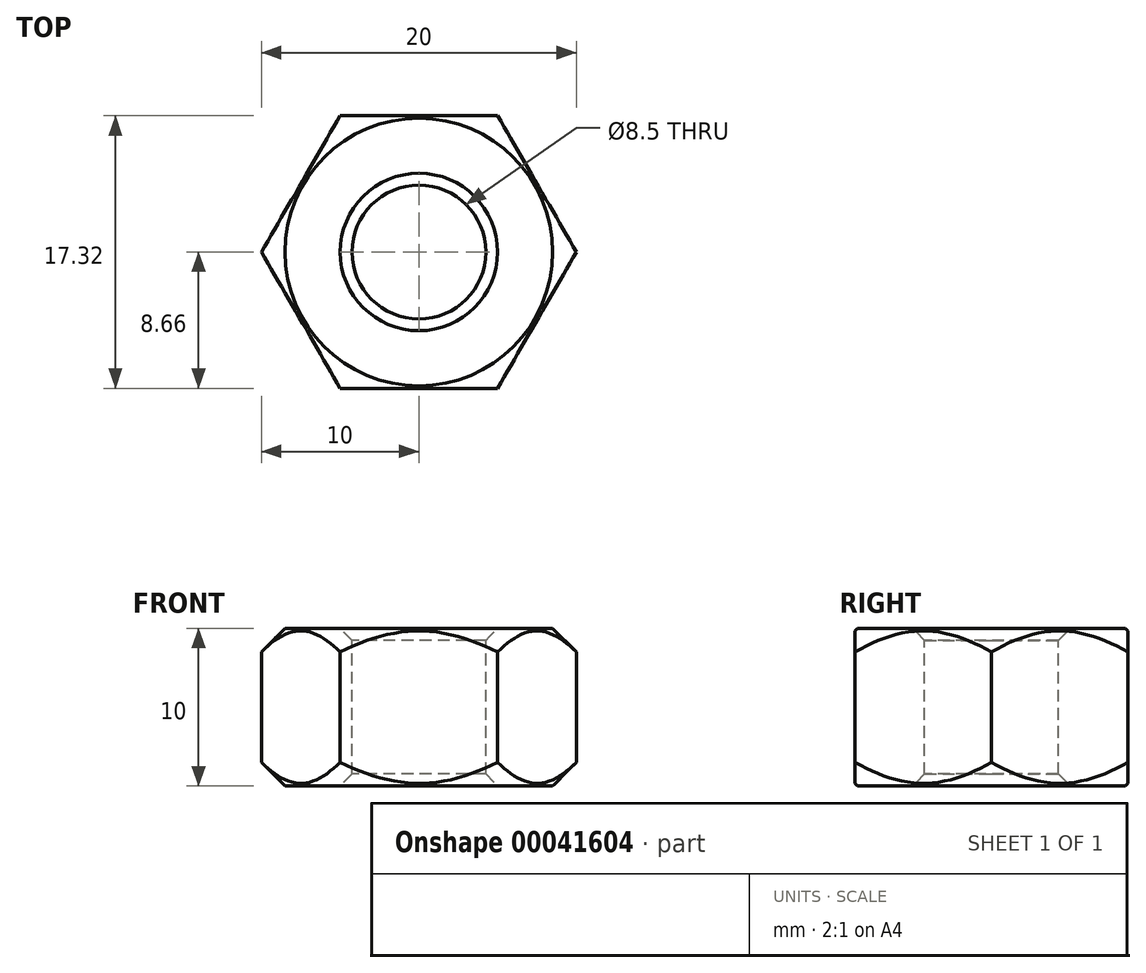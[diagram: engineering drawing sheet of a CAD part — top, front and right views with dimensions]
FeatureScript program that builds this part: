
annotation { "Feature Type Name" : "Feature", "Feature Type Description" : "" }
export const myFeature = defineFeature(function(context is Context, id is Id, definition is map)
    precondition{}
    {
        {
            var Q0;
            Q0=qCreatedBy(makeId("Front.planeOp"),FACE);
            var sketch = newSketch(context, id + "F0", { "sketchPlane" : qUnion([Q0])});
            skLineSegment(sketch, "E0.rect.bottom", {"start": v(10, 5) * mm, "end": v(-10, 5) * mm, "construction": true});
            skLineSegment(sketch, "E0.rect.top", {"start": v(10, -5) * mm, "end": v(-10, -5) * mm, "construction": true});
            skLineSegment(sketch, "E0.rect.left", {"start": v(10, 5) * mm, "end": v(10, -5) * mm});
            skLineSegment(sketch, "E0.rect.right", {"start": v(-10, 5) * mm, "end": v(-10, -5) * mm});
            skPoint(sketch, "E0.rect.middle", {"position": v(0, 0) * mm});
            skLineSegment(sketch, "E1", {"start": v(-5, 5) * mm, "end": v(-4.25, 4.25) * mm});
            skLineSegment(sketch, "E2", {"start": v(-4.25, 4.25) * mm, "end": v(-4.25, -4.25) * mm});
            skLineSegment(sketch, "E3", {"start": v(-4.25, -4.25) * mm, "end": v(-5, -5) * mm});
            skLineSegment(sketch, "E4", {"start": v(5, 5) * mm, "end": v(4.25, 4.25) * mm});
            skLineSegment(sketch, "E5", {"start": v(4.25, 4.25) * mm, "end": v(4.25, -4.25) * mm});
            skLineSegment(sketch, "E6", {"start": v(4.25, -4.25) * mm, "end": v(5, -5) * mm});
            skLineSegment(sketch, "E7", {"start": v(-10, 5) * mm, "end": v(-5, 5) * mm});
            skLineSegment(sketch, "E8", {"start": v(5, 5) * mm, "end": v(10, 5) * mm});
            skLineSegment(sketch, "E9", {"start": v(-4.25, 4.25) * mm, "end": v(4.25, 4.25) * mm, "construction": true});
            skLineSegment(sketch, "E10", {"start": v(-4.25, -4.25) * mm, "end": v(4.25, -4.25) * mm, "construction": true});
            skLineSegment(sketch, "E11", {"start": v(-5, -5) * mm, "end": v(-10, -5) * mm});
            skLineSegment(sketch, "E12", {"start": v(5, -5) * mm, "end": v(10, -5) * mm});
            skLineSegment(sketch, "E13", {"start": v(0, 5) * mm, "end": v(0, -5) * mm});
            skSolve(sketch);
        }
        {
            var Q0;
            Q0=makeQuery(id+"F0.imprint","IMPRINT",FACE,{"disambiguationData":[TD([[makeQuery(id+"F0.imprint","IMPRINT",EDGE,{"derivedFrom":sQuery(id+"F0.wireOp",EDGE,"E0.rect.right")}),1.0]])]});
            var Q1;
            Q1=sQuery(id+"F0.wireOp",EDGE,"E13");
            revolve(context, id + "F1", {"entities" : qUnion([Q0]), "axis" : qUnion([Q1]), "revolveType" : RevolveType.FULL});
        }
        {
            var Q0;
            Q0=makeQuery(id+"F1.opRevolve","SWEPT_EDGE",EDGE,{"disambiguationData":[OSD([sQuery(id+"F0.wireOp",EDGE,"E0.rect.right"),sQuery(id+"F0.wireOp",EDGE,"E7")])]});
            var Q1;
            Q1=makeQuery(id+"F1.opRevolve","SWEPT_EDGE",EDGE,{"disambiguationData":[OSD([sQuery(id+"F0.wireOp",EDGE,"E0.rect.right"),sQuery(id+"F0.wireOp",EDGE,"E11")])]});
            chamfer(context, id + "F2", {"entities" : qUnion([Q0, Q1]), "width" : 1.5 * mm, "tangentPropagation" : true});
        }
        {
            var Q0;
            Q0=makeQuery(id+"F1.opRevolve","SWEPT_FACE",FACE,{"disambiguationData":[OSD([sQuery(id+"F0.wireOp",EDGE,"E7")])]});
            var sketch = newSketch(context, id + "F3", { "sketchPlane" : qUnion([Q0])});
            skCircle(sketch, "E14.0", {"center": v(0, 0) * mm, "radius": 5 * mm});
            skCircle(sketch, "E15.cCircle", {"center": v(0, 0) * mm, "radius": 8.66 * mm, "construction": true});
            skLineSegment(sketch, "E15.0", {"start": v(-5, 8.66) * mm, "end": v(5, 8.66) * mm});
            skLineSegment(sketch, "E15.1", {"start": v(5, 8.66) * mm, "end": v(10, 0) * mm});
            skLineSegment(sketch, "E15.2", {"start": v(10, 0) * mm, "end": v(5, -8.66) * mm});
            skLineSegment(sketch, "E15.3", {"start": v(5, -8.66) * mm, "end": v(-5, -8.66) * mm});
            skLineSegment(sketch, "E15.4", {"start": v(-5, -8.66) * mm, "end": v(-10, 0) * mm});
            skLineSegment(sketch, "E15.5", {"start": v(-10, 0) * mm, "end": v(-5, 8.66) * mm});
            skPoint(sketch, "E15.0.midPoint", {"position": v(0, 8.66) * mm});
            skCircle(sketch, "E16.0", {"center": v(0, 0) * mm, "radius": 10 * mm});
            skSolve(sketch);
        }
        {
            var Q0;
            {var subQ1=sQuery(id+"F3.wireOp",EDGE,"E15.0");Q0=makeQuery(id+"F3.imprint","IMPRINT",FACE,{"disambiguationData":[TD([[makeQuery(id+"F3.imprint","IMPRINT",EDGE,{"derivedFrom":subQ1}),1.0]])]});}
            var Q1;
            {var subQ1=sQuery(id+"F3.wireOp",EDGE,"E15.5");Q1=makeQuery(id+"F3.imprint","IMPRINT",FACE,{"disambiguationData":[TD([[makeQuery(id+"F3.imprint","IMPRINT",EDGE,{"derivedFrom":subQ1}),1.0]])]});}
            var Q2;
            {var subQ1=sQuery(id+"F3.wireOp",EDGE,"E15.4");Q2=makeQuery(id+"F3.imprint","IMPRINT",FACE,{"disambiguationData":[TD([[makeQuery(id+"F3.imprint","IMPRINT",EDGE,{"derivedFrom":subQ1}),1.0]])]});}
            var Q3;
            {var subQ1=sQuery(id+"F3.wireOp",EDGE,"E15.3");Q3=makeQuery(id+"F3.imprint","IMPRINT",FACE,{"disambiguationData":[TD([[makeQuery(id+"F3.imprint","IMPRINT",EDGE,{"derivedFrom":subQ1}),1.0]])]});}
            var Q4;
            {var subQ1=sQuery(id+"F3.wireOp",EDGE,"E15.2");Q4=makeQuery(id+"F3.imprint","IMPRINT",FACE,{"disambiguationData":[TD([[makeQuery(id+"F3.imprint","IMPRINT",EDGE,{"derivedFrom":subQ1}),1.0]])]});}
            var Q5;
            {var subQ1=sQuery(id+"F3.wireOp",EDGE,"E15.1");Q5=makeQuery(id+"F3.imprint","IMPRINT",FACE,{"disambiguationData":[TD([[makeQuery(id+"F3.imprint","IMPRINT",EDGE,{"derivedFrom":subQ1}),1.0]])]});}
            extrude(context, id + "F4", {"entities" : qUnion([Q0, Q1, Q2, Q3, Q4, Q5]), "operationType" : NewBodyOperationType.REMOVE, "endBound" : BoundingType.THROUGH_ALL, "oppositeDirection" : true, "depth" : 25 * mm});
        }
    });
